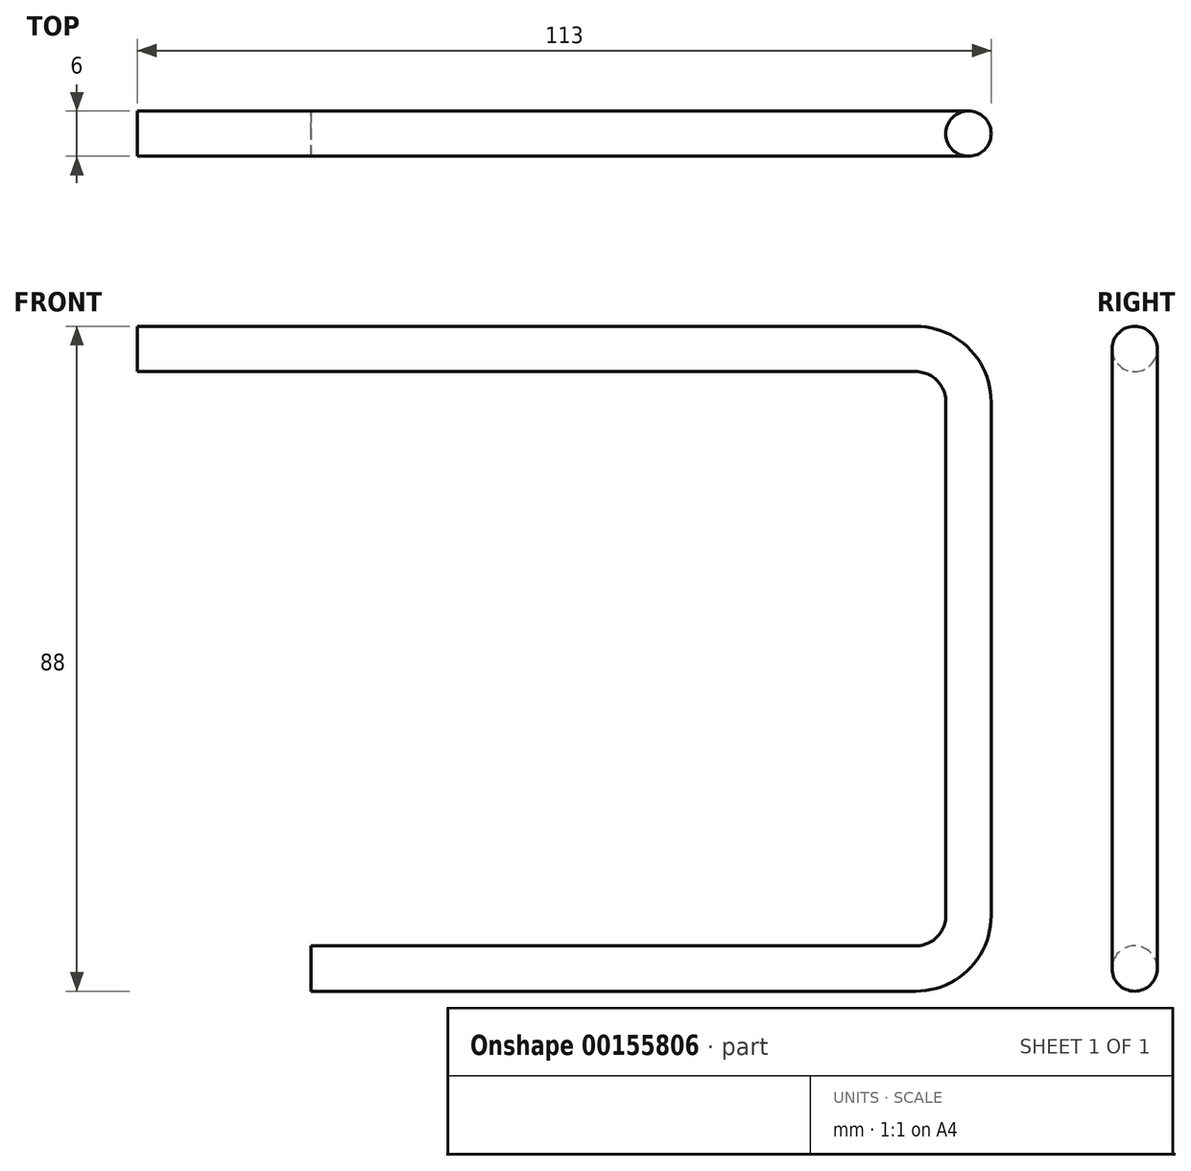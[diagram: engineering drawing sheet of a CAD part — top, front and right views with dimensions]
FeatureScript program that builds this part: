
annotation { "Feature Type Name" : "Feature", "Feature Type Description" : "" }
export const myFeature = defineFeature(function(context is Context, id is Id, definition is map)
    precondition{}
    {
        {
            var Q0;
            Q0=qCreatedBy(makeId("Front.planeOp"),FACE);
            var sketch = newSketch(context, id + "F0", { "sketchPlane" : qUnion([Q0])});
            skLineSegment(sketch, "E0", {"start": v(0, 0) * mm, "end": v(80, 0) * mm});
            skArc(sketch, "E1", {"start": v(80, 0) * mm, "mid": v(84.95, 2.05) * mm, "end": v(87, 7) * mm});
            skLineSegment(sketch, "E2", {"start": v(87, 7) * mm, "end": v(87, 75) * mm});
            skArc(sketch, "E3", {"start": v(87, 75) * mm, "mid": v(84.95, 79.95) * mm, "end": v(80, 82) * mm});
            skLineSegment(sketch, "E4", {"start": v(80, 82) * mm, "end": v(-23, 82) * mm});
            skSolve(sketch);
        }
        {
            var Q0;
            Q0=qCreatedBy(makeId("Right.planeOp"),FACE);
            var sketch = newSketch(context, id + "F1", { "sketchPlane" : qUnion([Q0])});
            skCircle(sketch, "E5", {"center": v(0, 0) * mm, "radius": 3 * mm});
            skSolve(sketch);
        }
        {
            var Q0;
            Q0=makeQuery(id+"F1.imprint","IMPRINT",FACE,{"disambiguationData":[TD([[makeQuery(id+"F1.imprint","IMPRINT",EDGE,{"derivedFrom":sQuery(id+"F1.wireOp",EDGE,"E5")}),1.0]])]});
            var Q1;
            Q1=sQuery(id+"F0.wireOp",EDGE,"E4");
            var Q2;
            Q2=sQuery(id+"F0.wireOp",EDGE,"E0");
            var Q3;
            Q3=sQuery(id+"F0.wireOp",EDGE,"E1");
            var Q4;
            Q4=sQuery(id+"F0.wireOp",EDGE,"E2");
            var Q5;
            Q5=sQuery(id+"F0.wireOp",EDGE,"E3");
            sweep(context, id + "F2", {"profiles" : qUnion([Q0]), "path" : qUnion([Q1, Q2, Q3, Q4, Q5])});
        }
    });
